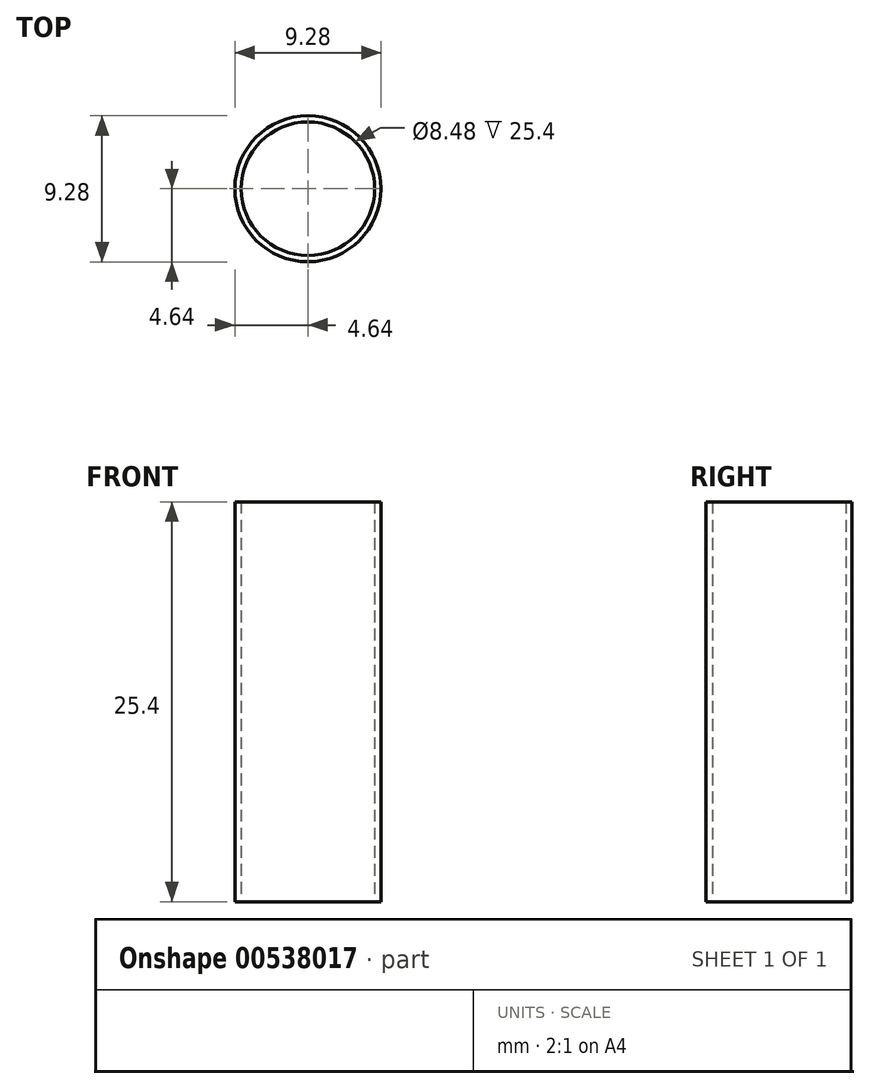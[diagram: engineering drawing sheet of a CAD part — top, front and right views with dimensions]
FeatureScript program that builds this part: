
annotation { "Feature Type Name" : "Feature", "Feature Type Description" : "" }
export const myFeature = defineFeature(function(context is Context, id is Id, definition is map)
    precondition{}
    {
        {
            var Q0;
            Q0=qCreatedBy(makeId("Top.planeOp"),FACE);
            var sketch = newSketch(context, id + "F0", { "sketchPlane" : qUnion([Q0])});
            skCircle(sketch, "E0", {"center": v(0, 0) * mm, "radius": 4.64 * mm});
            skCircle(sketch, "E1", {"center": v(0, 0) * mm, "radius": 4.24 * mm});
            skSolve(sketch);
        }
        {
            var Q0;
            Q0 = qSketchRegion(id + "F0", true);
            extrude(context, id + "F1", {"entities" : qUnion([Q0]), "depth" : 25.4 * mm, "offsetDistance" : 25.4 * mm});
        }
    });
